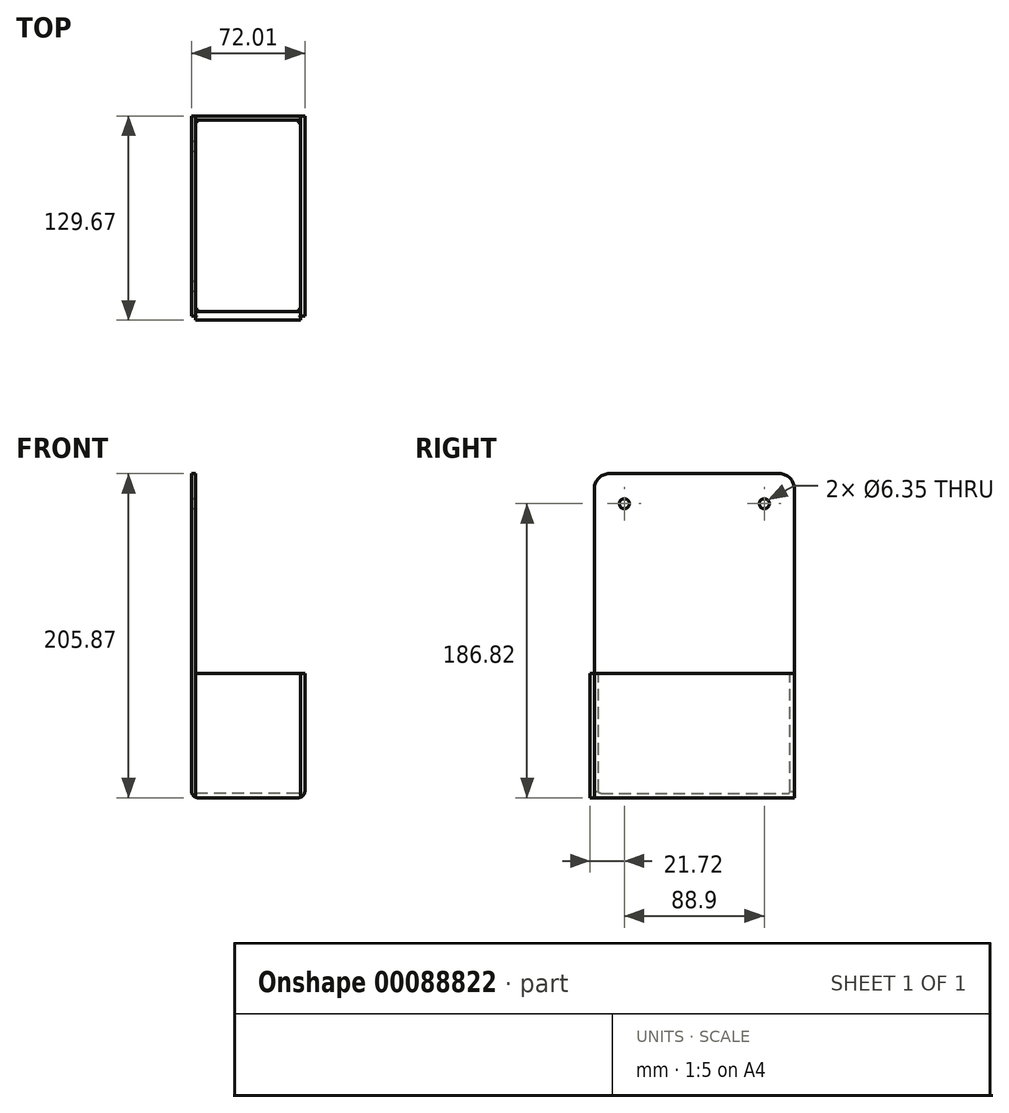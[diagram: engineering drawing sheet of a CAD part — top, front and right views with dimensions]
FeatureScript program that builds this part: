
annotation { "Feature Type Name" : "Feature", "Feature Type Description" : "" }
export const myFeature = defineFeature(function(context is Context, id is Id, definition is map)
    precondition{}
    {
        {
            var Q0;
            Q0=qCreatedBy(makeId("Front.planeOp"),FACE);
            var sketch = newSketch(context, id + "F0", { "sketchPlane" : qUnion([Q0])});
            skLineSegment(sketch, "E0.bottom", {"start": v(1.52, 0) * mm, "end": v(65.15, 0) * mm});
            skLineSegment(sketch, "E0.left", {"start": v(0, 1.52) * mm, "end": v(0, 76.2) * mm});
            skLineSegment(sketch, "E0.right", {"start": v(66.68, 1.52) * mm, "end": v(66.67, 76.2) * mm});
            skLineSegment(sketch, "E1", {"start": v(0, 76.2) * mm, "end": v(0, 203.2) * mm});
            skLineSegment(sketch, "E2.0", {"start": v(-2.67, 76.2) * mm, "end": v(-2.67, 203.2) * mm});
            skLineSegment(sketch, "E2.1", {"start": v(-2.67, 1.52) * mm, "end": v(-2.67, 76.2) * mm});
            skLineSegment(sketch, "E2.2", {"start": v(1.52, -2.67) * mm, "end": v(65.15, -2.67) * mm});
            skLineSegment(sketch, "E2.3", {"start": v(69.34, 1.52) * mm, "end": v(69.34, 76.2) * mm});
            skPoint(sketch, "E3.visualSharp", {"position": v(0, 0) * mm});
            skArc(sketch, "E3.filletArc", {"start": v(0, 1.52) * mm, "mid": v(0.45, 0.45) * mm, "end": v(1.52, 0) * mm});
            skPoint(sketch, "E4.visualSharp", {"position": v(66.68, 0) * mm});
            skArc(sketch, "E4.filletArc", {"start": v(65.15, 0) * mm, "mid": v(66.23, 0.45) * mm, "end": v(66.68, 1.52) * mm});
            skPoint(sketch, "E5.visualSharp", {"position": v(-2.67, -2.67) * mm});
            skArc(sketch, "E6.filletArc", {"start": v(-2.67, 1.52) * mm, "mid": v(-1.44, -1.44) * mm, "end": v(1.52, -2.67) * mm});
            skPoint(sketch, "E7.visualSharp", {"position": v(69.34, -2.67) * mm});
            skArc(sketch, "E7.filletArc", {"start": v(65.15, -2.67) * mm, "mid": v(68.11, -1.44) * mm, "end": v(69.34, 1.52) * mm});
            skLineSegment(sketch, "E8", {"start": v(69.34, 76.2) * mm, "end": v(66.67, 76.2) * mm});
            skLineSegment(sketch, "E9", {"start": v(-2.67, 203.2) * mm, "end": v(0, 203.2) * mm});
            skSolve(sketch);
        }
        {
            var Q0;
            Q0=makeQuery(id+"F0.imprint","IMPRINT",FACE,{"disambiguationData":[TD([[makeQuery(id+"F0.imprint","IMPRINT",EDGE,{"derivedFrom":sQuery(id+"F0.wireOp",EDGE,"E0.bottom")}),-1.0]])]});
            extrude(context, id + "F1", {"entities" : qUnion([Q0]), "endBound" : BoundingType.SYMMETRIC, "depth" : 127 * mm});
        }
        {
            var Q0;
            Q0=makeQuery(id+"F1.opExtrude","CAP_FACE",FACE,{"disambiguationData":[OSD([sQuery(id+"F0.wireOp",EDGE,"E0.bottom"),sQuery(id+"F0.wireOp",EDGE,"E0.left"),sQuery(id+"F0.wireOp",EDGE,"E0.right"),sQuery(id+"F0.wireOp",EDGE,"E1"),sQuery(id+"F0.wireOp",EDGE,"E2.0"),sQuery(id+"F0.wireOp",EDGE,"E2.1"),sQuery(id+"F0.wireOp",EDGE,"E2.2"),sQuery(id+"F0.wireOp",EDGE,"E2.3"),sQuery(id+"F0.wireOp",EDGE,"E3.filletArc"),sQuery(id+"F0.wireOp",EDGE,"E4.filletArc"),sQuery(id+"F0.wireOp",EDGE,"E6.filletArc"),sQuery(id+"F0.wireOp",EDGE,"E7.filletArc"),sQuery(id+"F0.wireOp",EDGE,"E8"),sQuery(id+"F0.wireOp",EDGE,"E9")])],"isStart":false});
            var sketch = newSketch(context, id + "F2", { "sketchPlane" : qUnion([Q0])});
            skLineSegment(sketch, "E10", {"start": v(66.65, 76.2) * mm, "end": v(0.03, 76.2) * mm});
            skLineSegment(sketch, "E11.0", {"start": v(0.03, -1.14) * mm, "end": v(0.03, 76.2) * mm});
            skLineSegment(sketch, "E12.0", {"start": v(1.55, -2.67) * mm, "end": v(65.13, -2.67) * mm});
            skPoint(sketch, "E13.orphan", {"position": v(1.52, -2.67) * mm});
            skPoint(sketch, "E14.visualSharp", {"position": v(0.03, -2.67) * mm});
            skArc(sketch, "E14.filletArc", {"start": v(0.03, -1.14) * mm, "mid": v(0.47, -2.22) * mm, "end": v(1.55, -2.67) * mm});
            skLineSegment(sketch, "E15.0", {"start": v(66.65, -1.14) * mm, "end": v(66.65, 76.2) * mm});
            skPoint(sketch, "E16.visualSharp", {"position": v(66.65, -2.67) * mm});
            skArc(sketch, "E16.filletArc", {"start": v(65.13, -2.67) * mm, "mid": v(66.2, -2.22) * mm, "end": v(66.65, -1.14) * mm});
            skSolve(sketch);
        }
        {
            var Q0;
            Q0 = qSketchRegion(id + "F2", true);
            extrude(context, id + "F3", {"entities" : qUnion([Q0]), "oppositeDirection" : true, "depth" : 2.67 * mm});
        }
        {
            var Q0;
            Q0=makeQuery(id+"F3.opExtrude","SWEPT_BODY",BODY,{"disambiguationData":[OSD([sQuery(id+"F2.wireOp",EDGE,"E10"),sQuery(id+"F2.wireOp",EDGE,"E11.0"),sQuery(id+"F2.wireOp",EDGE,"E12.0"),sQuery(id+"F2.wireOp",EDGE,"E14.filletArc"),sQuery(id+"F2.wireOp",EDGE,"E15.0"),sQuery(id+"F2.wireOp",EDGE,"E16.filletArc")])]});
            var Q1;
            Q1=qCreatedBy(makeId("Front.planeOp"),FACE);
            mirror(context, id + "F4", {"operationType" : NewBodyOperationType.ADD, "entities" : qUnion([Q0]), "mirrorPlane" : qUnion([Q1])});
        }
        {
            var Q0;
            Q0=makeQuery(id+"F4.boolean.opBoolean","INTERSECT",EDGE,{"derivedFrom":[makeQuery(id+"F1.opExtrude","SWEPT_FACE",FACE,{"disambiguationData":[OSD([sQuery(id+"F0.wireOp",EDGE,"E0.bottom")])]}),makeQuery(id+"F3.opExtrude","CAP_FACE",FACE,{"disambiguationData":[OSD([sQuery(id+"F2.wireOp",EDGE,"E10"),sQuery(id+"F2.wireOp",EDGE,"E11.0"),sQuery(id+"F2.wireOp",EDGE,"E12.0"),sQuery(id+"F2.wireOp",EDGE,"E14.filletArc"),sQuery(id+"F2.wireOp",EDGE,"E15.0"),sQuery(id+"F2.wireOp",EDGE,"E16.filletArc")])],"isStart":false})]});
            fillet(context, id + "F5", {"entities" : qUnion([Q0]), "radius" : 1.52 * mm, "allowEdgeOverflow" : false});
        }
        {
            var Q0;
            Q0=makeQuery(id+"F4.boolean.opBoolean","INTERSECT",EDGE,{"derivedFrom":[makeQuery(id+"F1.opExtrude","SWEPT_FACE",FACE,{"disambiguationData":[OSD([sQuery(id+"F0.wireOp",EDGE,"E0.bottom")])]}),makeQuery(id+"F4.opPattern","COPY",FACE,{"derivedFrom":makeQuery(id+"F3.opExtrude","CAP_FACE",FACE,{"disambiguationData":[OSD([sQuery(id+"F2.wireOp",EDGE,"E10"),sQuery(id+"F2.wireOp",EDGE,"E11.0"),sQuery(id+"F2.wireOp",EDGE,"E12.0"),sQuery(id+"F2.wireOp",EDGE,"E14.filletArc"),sQuery(id+"F2.wireOp",EDGE,"E15.0"),sQuery(id+"F2.wireOp",EDGE,"E16.filletArc")])],"isStart":false}),"instanceName":"1"})]});
            fillet(context, id + "F6", {"entities" : qUnion([Q0]), "radius" : 1.52 * mm, "allowEdgeOverflow" : false});
        }
        {
            var Q0;
            Q0=makeQuery(id+"F1.opExtrude","SWEPT_FACE",FACE,{"disambiguationData":[OSD([sQuery(id+"F0.wireOp",EDGE,"E0.left"),sQuery(id+"F0.wireOp",EDGE,"E1")])]});
            var sketch = newSketch(context, id + "F7", { "sketchPlane" : qUnion([Q0])});
            skPoint(sketch, "E17", {"position": v(-44.45, 184.15) * mm});
            skPoint(sketch, "E18", {"position": v(44.45, 184.15) * mm});
            skSolve(sketch);
        }
        {
            var Q0;
            Q0=sQuery(id+"F7.wireOp",VERTEX,"E17");
            var Q1;
            Q1=sQuery(id+"F7.wireOp",VERTEX,"E18");
            var Q2;
            Q2=makeQuery(id+"F1.opExtrude","SWEPT_BODY",BODY,{"disambiguationData":[OSD([sQuery(id+"F0.wireOp",EDGE,"E0.bottom"),sQuery(id+"F0.wireOp",EDGE,"E0.left"),sQuery(id+"F0.wireOp",EDGE,"E0.right"),sQuery(id+"F0.wireOp",EDGE,"E1"),sQuery(id+"F0.wireOp",EDGE,"E2.0"),sQuery(id+"F0.wireOp",EDGE,"E2.1"),sQuery(id+"F0.wireOp",EDGE,"E2.2"),sQuery(id+"F0.wireOp",EDGE,"E2.3"),sQuery(id+"F0.wireOp",EDGE,"E3.filletArc"),sQuery(id+"F0.wireOp",EDGE,"E4.filletArc"),sQuery(id+"F0.wireOp",EDGE,"E6.filletArc"),sQuery(id+"F0.wireOp",EDGE,"E7.filletArc"),sQuery(id+"F0.wireOp",EDGE,"E8"),sQuery(id+"F0.wireOp",EDGE,"E9")])]});
            hole(context, id + "F8", {"style" : HoleStyle.SIMPLE, "endStyle" : HoleEndStyle.THROUGH, "holeDiameter" : 6.35 * mm, "locations" : qUnion([Q0, Q1]), "scope" : qUnion([Q2]), "isTappedThrough" : true});
        }
        {
            var Q0;
            Q0=makeQuery(id+"F1.opExtrude","CAP_EDGE",EDGE,{"disambiguationData":[OSD([sQuery(id+"F0.wireOp",EDGE,"E9")])],"isStart":false});
            var Q1;
            Q1=makeQuery(id+"F1.opExtrude","CAP_EDGE",EDGE,{"disambiguationData":[OSD([sQuery(id+"F0.wireOp",EDGE,"E9")])],"isStart":true});
            fillet(context, id + "F9", {"entities" : qUnion([Q0, Q1]), "radius" : 9.52 * mm, "tangentPropagation" : true, "allowEdgeOverflow" : false});
        }
        {
            var Q0;
            Q0 = qSketchRegion(id + "F2", true);
            extrude(context, id + "F10", {"entities" : qUnion([Q0]), "operationType" : NewBodyOperationType.ADD, "depth" : 2.67 * mm});
        }
    });
